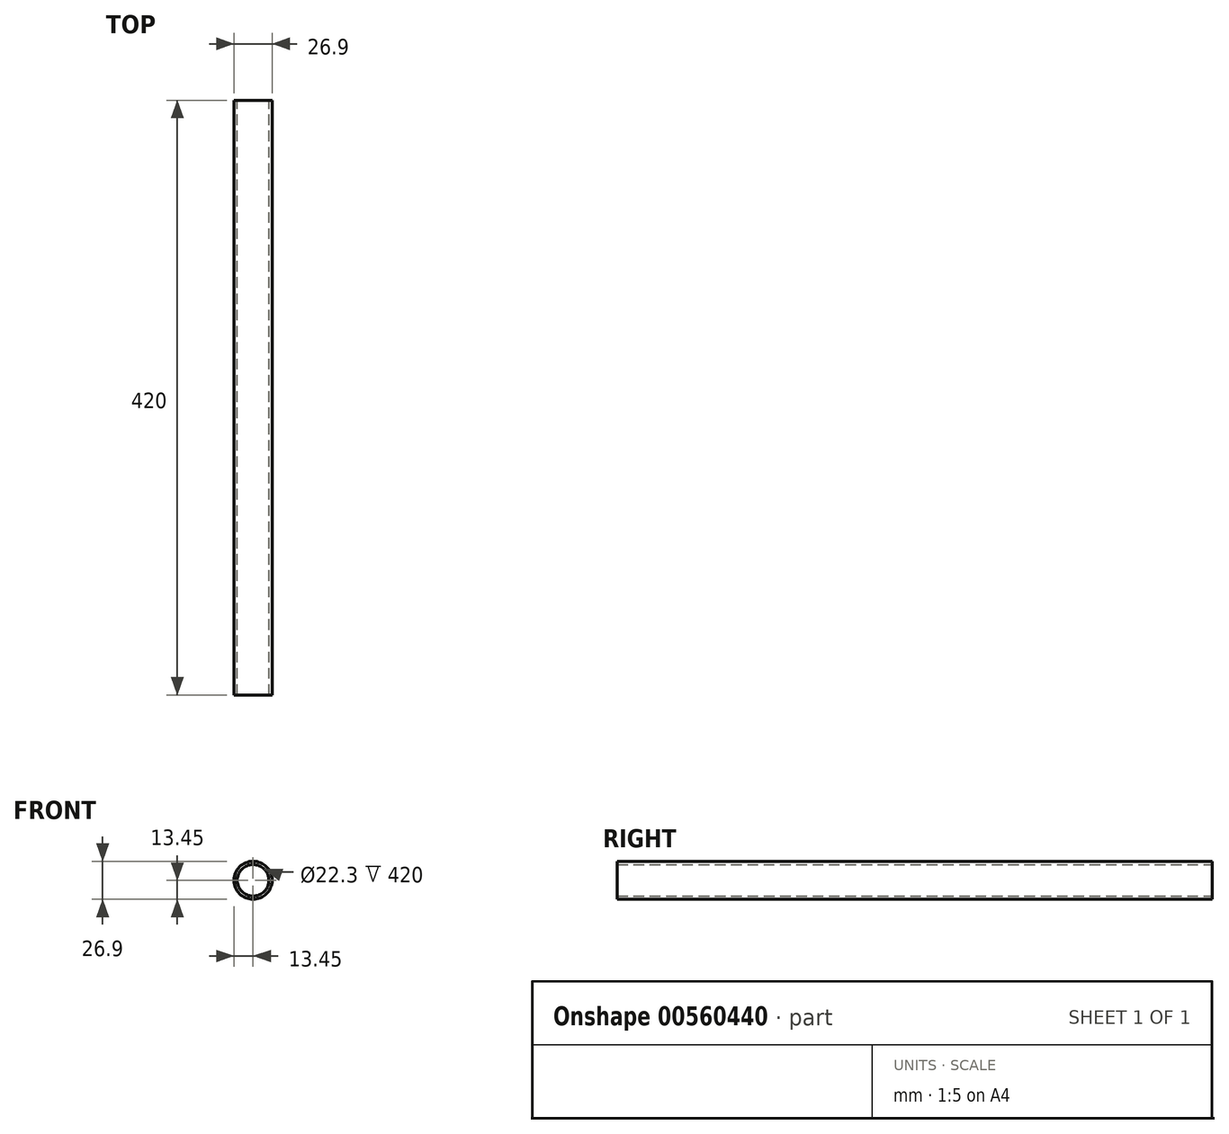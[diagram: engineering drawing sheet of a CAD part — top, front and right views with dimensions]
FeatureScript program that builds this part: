
annotation { "Feature Type Name" : "Feature", "Feature Type Description" : "" }
export const myFeature = defineFeature(function(context is Context, id is Id, definition is map)
    precondition{}
    {
        {
            var Q0;
            Q0=qCreatedBy(makeId("Front.planeOp"),FACE);
            var sketch = newSketch(context, id + "F0", { "sketchPlane" : qUnion([Q0])});
            skCircle(sketch, "E0", {"center": v(0, 0) * mm, "radius": 13.45 * mm});
            skCircle(sketch, "E1.0", {"center": v(0, 0) * mm, "radius": 11.15 * mm});
            skSolve(sketch);
        }
        {
            var Q0;
            Q0=makeQuery(id+"F0.imprint","IMPRINT",FACE,{"disambiguationData":[TD([[makeQuery(id+"F0.imprint","IMPRINT",EDGE,{"derivedFrom":sQuery(id+"F0.wireOp",EDGE,"E0")}),1.0]])]});
            extrude(context, id + "F1", {"entities" : qUnion([Q0]), "endBound" : BoundingType.SYMMETRIC, "depth" : 420 * mm, "offsetDistance" : 25 * mm});
        }
    });
